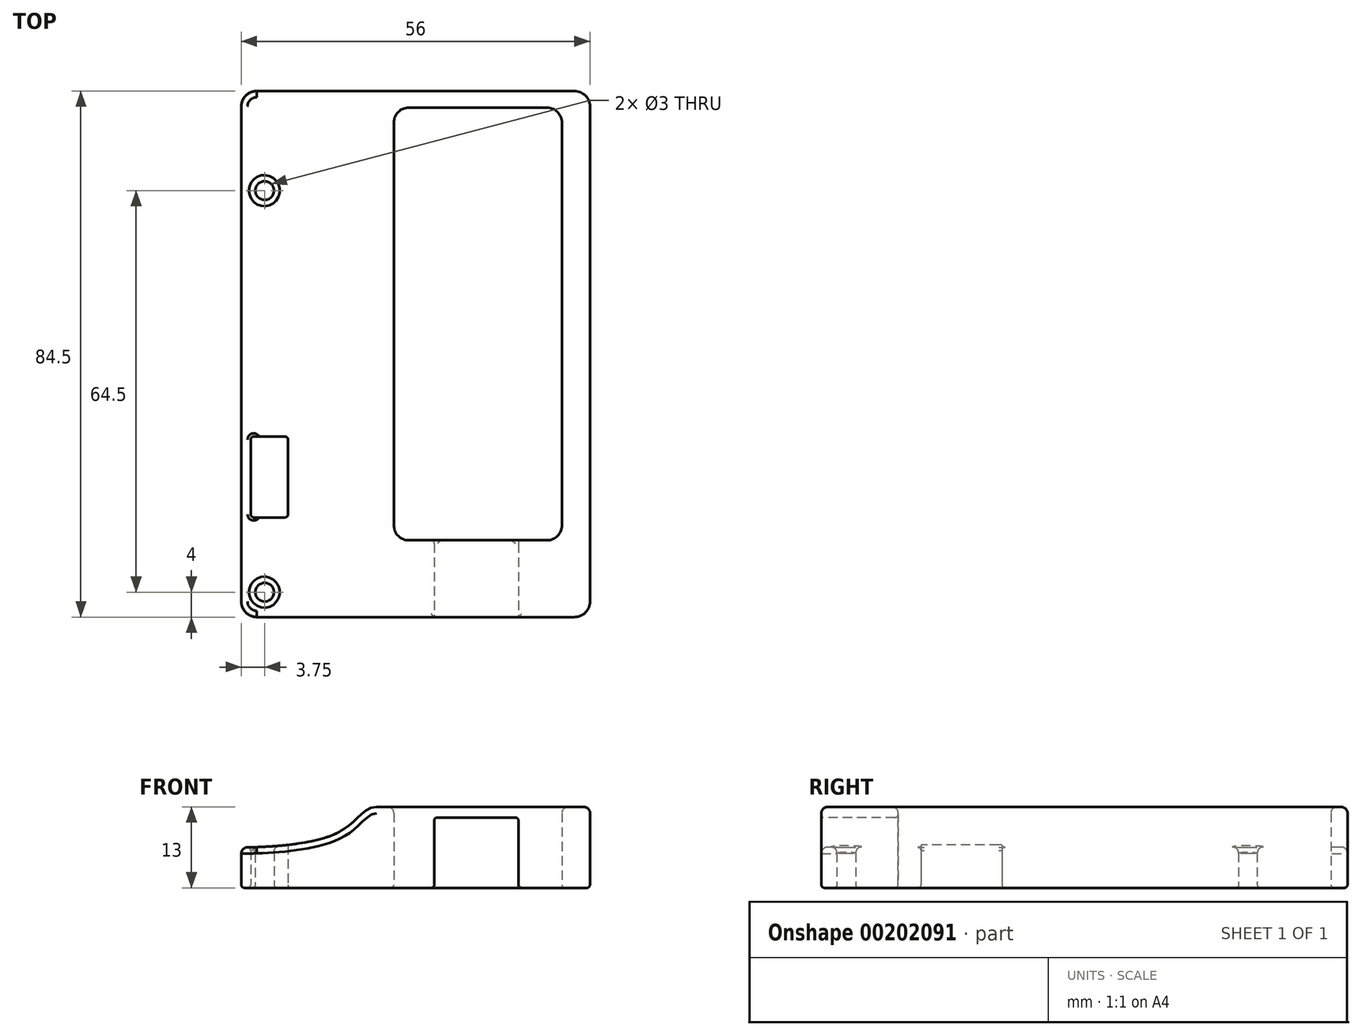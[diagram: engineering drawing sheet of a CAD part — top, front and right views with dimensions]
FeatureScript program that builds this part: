
annotation { "Feature Type Name" : "Feature", "Feature Type Description" : "" }
export const myFeature = defineFeature(function(context is Context, id is Id, definition is map)
    precondition{}
    {
        {
            var Q0;
            Q0=qCreatedBy(makeId("Top.planeOp"),FACE);
            var sketch = newSketch(context, id + "F0", { "sketchPlane" : qUnion([Q0])});
            skLineSegment(sketch, "E0.bottom", {"start": v(25.5, 36.25) * mm, "end": v(-25.5, 36.25) * mm});
            skLineSegment(sketch, "E0.top", {"start": v(25.5, -36.25) * mm, "end": v(-25.5, -36.25) * mm});
            skLineSegment(sketch, "E0.left", {"start": v(28, 33.75) * mm, "end": v(28, -33.75) * mm});
            skLineSegment(sketch, "E0.right", {"start": v(-28, 33.75) * mm, "end": v(-28, -33.75) * mm});
            skPoint(sketch, "E0.middle", {"position": v(0, 0) * mm});
            skPoint(sketch, "E1.visualSharp", {"position": v(-28, 36.25) * mm});
            skArc(sketch, "E1.filletArc", {"start": v(-25.5, 36.25) * mm, "mid": v(-27.27, 35.52) * mm, "end": v(-28, 33.75) * mm});
            skPoint(sketch, "E2.visualSharp", {"position": v(28, 36.25) * mm});
            skArc(sketch, "E2.filletArc", {"start": v(28, 33.75) * mm, "mid": v(27.27, 35.52) * mm, "end": v(25.5, 36.25) * mm});
            skPoint(sketch, "E3.visualSharp", {"position": v(28, -36.25) * mm});
            skArc(sketch, "E3.filletArc", {"start": v(25.5, -36.25) * mm, "mid": v(27.27, -35.52) * mm, "end": v(28, -33.75) * mm});
            skPoint(sketch, "E4.visualSharp", {"position": v(-28, -36.25) * mm});
            skArc(sketch, "E4.filletArc", {"start": v(-28, -33.75) * mm, "mid": v(-27.27, -35.52) * mm, "end": v(-25.5, -36.25) * mm});
            skLineSegment(sketch, "E5.bottom", {"start": v(24.25, 32.25) * mm, "end": v(-24.25, 32.25) * mm, "construction": true});
            skLineSegment(sketch, "E5.top", {"start": v(24.25, -32.25) * mm, "end": v(-24.25, -32.25) * mm, "construction": true});
            skLineSegment(sketch, "E5.left", {"start": v(24.25, 32.25) * mm, "end": v(24.25, -32.25) * mm, "construction": true});
            skLineSegment(sketch, "E5.right", {"start": v(-24.25, 32.25) * mm, "end": v(-24.25, -32.25) * mm, "construction": true});
            skCircle(sketch, "E6", {"center": v(-24.25, 32.25) * mm, "radius": 1.5 * mm});
            skCircle(sketch, "E7", {"center": v(24.25, 32.25) * mm, "radius": 1.5 * mm});
            skCircle(sketch, "E8", {"center": v(24.25, -32.25) * mm, "radius": 1.5 * mm});
            skCircle(sketch, "E9", {"center": v(-24.25, -32.25) * mm, "radius": 1.5 * mm});
            skLineSegment(sketch, "E10", {"start": v(-28, 33.75) * mm, "end": v(-28, 45.75) * mm});
            skLineSegment(sketch, "E11", {"start": v(-25.5, 48.25) * mm, "end": v(25.5, 48.25) * mm});
            skLineSegment(sketch, "E12", {"start": v(28, 45.75) * mm, "end": v(28, 33.75) * mm});
            skPoint(sketch, "E13.visualSharp", {"position": v(-28, 48.25) * mm});
            skArc(sketch, "E13.filletArc", {"start": v(-25.5, 48.25) * mm, "mid": v(-27.27, 47.52) * mm, "end": v(-28, 45.75) * mm});
            skPoint(sketch, "E14.visualSharp", {"position": v(28, 48.25) * mm});
            skArc(sketch, "E14.filletArc", {"start": v(28, 45.75) * mm, "mid": v(27.27, 47.52) * mm, "end": v(25.5, 48.25) * mm});
            skSolve(sketch);
        }
        {
            var Q0;
            Q0 = qSketchRegion(id + "F0", true);
            var Q1;
            Q1=makeQuery(id+"F0.imprint","IMPRINT",FACE,{"disambiguationData":[TD([[makeQuery(id+"F0.imprint","IMPRINT",EDGE,{"derivedFrom":sQuery(id+"F0.wireOp",EDGE,"E7")}),1.0]])]});
            var Q2;
            Q2=makeQuery(id+"F0.imprint","IMPRINT",FACE,{"disambiguationData":[TD([[makeQuery(id+"F0.imprint","IMPRINT",EDGE,{"derivedFrom":sQuery(id+"F0.wireOp",EDGE,"E8")}),1.0]])]});
            extrude(context, id + "F1", {"entities" : qUnion([Q0, Q1, Q2]), "depth" : 13 * mm});
        }
        {
            var Q0;
            Q0=makeQuery(id+"F1.opExtrude","SWEPT_FACE",FACE,{"disambiguationData":[OSD([sQuery(id+"F0.wireOp",EDGE,"E0.top")])]});
            var sketch = newSketch(context, id + "F2", { "sketchPlane" : qUnion([Q0])});
            skPoint(sketch, "E15.2.internal.snap0", {"position": v(-25.5, 6.5) * mm});
            skFitSpline(sketch, "E15", {"points": [v(-6.26, 13) * mm, v(-12.41, 8.9) * mm, v(-28, 6.5) * mm], "startDerivative": vector(-16.32, 0) * mm, "endDerivative": vector(-12.63, 0) * mm});
            skLineSegment(sketch, "E16.0", {"start": v(-28, 13) * mm, "end": v(-28, 6.5) * mm});
            skLineSegment(sketch, "E17", {"start": v(-28, 13) * mm, "end": v(-6.26, 13) * mm});
            skPoint(sketch, "E18.orphan", {"position": v(-28, 0) * mm});
            skSolve(sketch);
        }
        {
            var Q0;
            Q0 = qSketchRegion(id + "F2", true);
            extrude(context, id + "F3", {"entities" : qUnion([Q0]), "operationType" : NewBodyOperationType.REMOVE, "endBound" : BoundingType.THROUGH_ALL, "oppositeDirection" : true, "depth" : 25 * mm});
        }
        {
            var Q0;
            Q0=makeQuery(id+"F1.opExtrude","CAP_FACE",FACE,{"disambiguationData":[OSD([sQuery(id+"F0.wireOp",EDGE,"E0.top"),sQuery(id+"F0.wireOp",EDGE,"E0.left"),sQuery(id+"F0.wireOp",EDGE,"E0.right"),sQuery(id+"F0.wireOp",EDGE,"E3.filletArc"),sQuery(id+"F0.wireOp",EDGE,"E4.filletArc"),sQuery(id+"F0.wireOp",EDGE,"E6"),sQuery(id+"F0.wireOp",EDGE,"E7"),sQuery(id+"F0.wireOp",EDGE,"E8"),sQuery(id+"F0.wireOp",EDGE,"E9"),sQuery(id+"F0.wireOp",EDGE,"E10"),sQuery(id+"F0.wireOp",EDGE,"E11"),sQuery(id+"F0.wireOp",EDGE,"E12"),sQuery(id+"F0.wireOp",EDGE,"E13.filletArc"),sQuery(id+"F0.wireOp",EDGE,"E14.filletArc")])],"isStart":true});
            var sketch = newSketch(context, id + "F4", { "sketchPlane" : qUnion([Q0])});
            skLineSegment(sketch, "E19.bottom", {"start": v(3, 19.25) * mm, "end": v(16.5, 19.25) * mm});
            skLineSegment(sketch, "E19.top", {"start": v(3, 36.25) * mm, "end": v(16.5, 36.25) * mm});
            skLineSegment(sketch, "E19.left", {"start": v(3, 19.25) * mm, "end": v(3, 36.25) * mm});
            skLineSegment(sketch, "E19.right", {"start": v(16.5, 19.25) * mm, "end": v(16.5, 36.25) * mm});
            skPoint(sketch, "E19.middle", {"position": v(9.75, 27.75) * mm});
            skLineSegment(sketch, "E20.bottom", {"start": v(-3.5, -45.58) * mm, "end": v(23.5, -45.58) * mm});
            skLineSegment(sketch, "E20.top", {"start": v(-3.5, 23.92) * mm, "end": v(23.5, 23.92) * mm});
            skLineSegment(sketch, "E20.left", {"start": v(-3.5, -45.58) * mm, "end": v(-3.5, 23.92) * mm});
            skLineSegment(sketch, "E20.right", {"start": v(23.5, -45.58) * mm, "end": v(23.5, 23.92) * mm});
            skPoint(sketch, "E20.middle", {"position": v(10, -10.83) * mm});
            skSolve(sketch);
        }
        {
            var Q0;
            {var subQ0=sQuery(id+"F4.wireOp",EDGE,"E19.top");Q0=makeQuery(id+"F4.imprint","IMPRINT",FACE,{"disambiguationData":[TD([[makeQuery(id+"F4.imprint","IMPRINT",EDGE,{"derivedFrom":subQ0}),1.0]])]});}
            var Q1;
            {var subQ0=sQuery(id+"F4.wireOp",EDGE,"E19.bottom");Q1=makeQuery(id+"F4.imprint","IMPRINT",FACE,{"disambiguationData":[TD([[makeQuery(id+"F4.imprint","IMPRINT",EDGE,{"derivedFrom":subQ0}),1.0]])]});}
            extrude(context, id + "F5", {"entities" : qUnion([Q0, Q1]), "operationType" : NewBodyOperationType.REMOVE, "oppositeDirection" : true, "depth" : 11.3 * mm});
        }
        {
            var Q0;
            {var subQ2=sQuery(id+"F4.wireOp",EDGE,"E19.bottom");Q0=makeQuery(id+"F4.imprint","IMPRINT",FACE,{"disambiguationData":[TD([[makeQuery(id+"F4.imprint","IMPRINT",EDGE,{"derivedFrom":subQ2}),-1.0]])]});}
            var Q1;
            {var subQ0=sQuery(id+"F4.wireOp",EDGE,"E19.bottom");Q1=makeQuery(id+"F4.imprint","IMPRINT",FACE,{"disambiguationData":[TD([[makeQuery(id+"F4.imprint","IMPRINT",EDGE,{"derivedFrom":subQ0}),1.0]])]});}
            extrude(context, id + "F6", {"entities" : qUnion([Q0, Q1]), "operationType" : NewBodyOperationType.REMOVE, "endBound" : BoundingType.THROUGH_ALL, "oppositeDirection" : true, "depth" : 25 * mm});
        }
        {
            var Q0;
            Q0=makeQuery(id+"F6.boolean.opBoolean","COPY",EDGE,{"derivedFrom":makeQuery(id+"F6.opExtrude","SWEPT_EDGE",EDGE,{"disambiguationData":[OSD([sQuery(id+"F4.wireOp",EDGE,"E20.bottom"),sQuery(id+"F4.wireOp",EDGE,"E20.left")])]})});
            var Q1;
            Q1=makeQuery(id+"F6.boolean.opBoolean","COPY",EDGE,{"derivedFrom":makeQuery(id+"F6.opExtrude","SWEPT_EDGE",EDGE,{"disambiguationData":[OSD([sQuery(id+"F4.wireOp",EDGE,"E20.bottom"),sQuery(id+"F4.wireOp",EDGE,"E20.right")])]})});
            var Q2;
            Q2=makeQuery(id+"F6.boolean.opBoolean","COPY",EDGE,{"derivedFrom":makeQuery(id+"F6.opExtrude","SWEPT_EDGE",EDGE,{"disambiguationData":[OSD([sQuery(id+"F4.wireOp",EDGE,"E20.top"),sQuery(id+"F4.wireOp",EDGE,"E20.right")])]})});
            var Q3;
            Q3=makeQuery(id+"F6.boolean.opBoolean","COPY",EDGE,{"derivedFrom":makeQuery(id+"F6.opExtrude","SWEPT_EDGE",EDGE,{"disambiguationData":[OSD([sQuery(id+"F4.wireOp",EDGE,"E20.top"),sQuery(id+"F4.wireOp",EDGE,"E20.left")])]})});
            fillet(context, id + "F7", {"entities" : qUnion([Q0, Q1, Q2, Q3]), "radius" : 2.4 * mm, "tangentPropagation" : true, "allowEdgeOverflow" : false});
        }
        {
            var Q0;
            Q0=makeQuery(id+"F4.imprint","IMPRINT",FACE,{"disambiguationData":[TD([[makeQuery(id+"F4.imprint","IMPRINT",EDGE,{"derivedFrom":sQuery(id+"F4.wireOp",EDGE,"E20.bottom")}),-1.0]])]});
            var sketch = newSketch(context, id + "F8", { "sketchPlane" : qUnion([Q0])});
            skLineSegment(sketch, "E21.bottom", {"start": v(-26.5, 20.25) * mm, "end": v(-20.5, 20.25) * mm});
            skLineSegment(sketch, "E21.top", {"start": v(-26.5, 7.25) * mm, "end": v(-20.5, 7.25) * mm});
            skLineSegment(sketch, "E21.left", {"start": v(-26.5, 20.25) * mm, "end": v(-26.5, 7.25) * mm});
            skLineSegment(sketch, "E21.right", {"start": v(-20.5, 20.25) * mm, "end": v(-20.5, 7.25) * mm});
            skPoint(sketch, "E21.middle", {"position": v(-23.5, 13.75) * mm});
            skSolve(sketch);
        }
        {
            var Q0;
            Q0 = qSketchRegion(id + "F8", true);
            extrude(context, id + "F9", {"entities" : qUnion([Q0]), "operationType" : NewBodyOperationType.REMOVE, "endBound" : BoundingType.THROUGH_ALL, "oppositeDirection" : true, "depth" : 25 * mm});
        }
        {
            var Q0;
            Q0=makeQuery(id+"F6.boolean.opBoolean","INTERSECT",EDGE,{"derivedFrom":[makeQuery(id+"F5.boolean.opBoolean","COPY",FACE,{"derivedFrom":makeQuery(id+"F5.opExtrude","SWEPT_FACE",FACE,{"disambiguationData":[OSD([sQuery(id+"F4.wireOp",EDGE,"E19.left")])]})}),makeQuery(id+"F6.opExtrude","SWEPT_FACE",FACE,{"disambiguationData":[OSD([sQuery(id+"F4.wireOp",EDGE,"E20.top")])]})]});
            var Q1;
            Q1=makeQuery(id+"F6.boolean.opBoolean","INTERSECT",EDGE,{"derivedFrom":[makeQuery(id+"F5.boolean.opBoolean","COPY",FACE,{"derivedFrom":makeQuery(id+"F5.opExtrude","SWEPT_FACE",FACE,{"disambiguationData":[OSD([sQuery(id+"F4.wireOp",EDGE,"E19.right")])]})}),makeQuery(id+"F6.opExtrude","SWEPT_FACE",FACE,{"disambiguationData":[OSD([sQuery(id+"F4.wireOp",EDGE,"E20.top")])]})]});
            var Q2;
            Q2=makeQuery(id+"F5.boolean.opBoolean","COPY",EDGE,{"derivedFrom":makeQuery(id+"F5.opExtrude","SWEPT_EDGE",EDGE,{"disambiguationData":[OSD([sQuery(id+"F0.wireOp",EDGE,"E0.top"),sQuery(id+"F4.wireOp",EDGE,"E19.top"),sQuery(id+"F4.wireOp",EDGE,"E19.left")])]})});
            var Q3;
            Q3=makeQuery(id+"F5.boolean.opBoolean","COPY",EDGE,{"derivedFrom":makeQuery(id+"F5.opExtrude","SWEPT_EDGE",EDGE,{"disambiguationData":[OSD([sQuery(id+"F0.wireOp",EDGE,"E0.top"),sQuery(id+"F4.wireOp",EDGE,"E19.top"),sQuery(id+"F4.wireOp",EDGE,"E19.right")])]})});
            var Q4;
            Q4=makeQuery(id+"F1.opExtrude","CAP_FACE",FACE,{"disambiguationData":[OSD([sQuery(id+"F0.wireOp",EDGE,"E0.top"),sQuery(id+"F0.wireOp",EDGE,"E0.left"),sQuery(id+"F0.wireOp",EDGE,"E0.right"),sQuery(id+"F0.wireOp",EDGE,"E3.filletArc"),sQuery(id+"F0.wireOp",EDGE,"E4.filletArc"),sQuery(id+"F0.wireOp",EDGE,"E6"),sQuery(id+"F0.wireOp",EDGE,"E9"),sQuery(id+"F0.wireOp",EDGE,"E10"),sQuery(id+"F0.wireOp",EDGE,"E11"),sQuery(id+"F0.wireOp",EDGE,"E12"),sQuery(id+"F0.wireOp",EDGE,"E13.filletArc"),sQuery(id+"F0.wireOp",EDGE,"E14.filletArc")])],"isStart":true});
            var Q5;
            Q5=makeQuery(id+"F9.boolean.opBoolean","COPY",EDGE,{"derivedFrom":makeQuery(id+"F9.opExtrude","SWEPT_EDGE",EDGE,{"disambiguationData":[OSD([sQuery(id+"F8.wireOp",EDGE,"E21.top"),sQuery(id+"F8.wireOp",EDGE,"E21.right")])]})});
            var Q6;
            Q6=makeQuery(id+"F9.boolean.opBoolean","COPY",EDGE,{"derivedFrom":makeQuery(id+"F9.opExtrude","SWEPT_EDGE",EDGE,{"disambiguationData":[OSD([sQuery(id+"F8.wireOp",EDGE,"E21.top"),sQuery(id+"F8.wireOp",EDGE,"E21.left")])]})});
            var Q7;
            Q7=makeQuery(id+"F9.boolean.opBoolean","COPY",EDGE,{"derivedFrom":makeQuery(id+"F9.opExtrude","SWEPT_EDGE",EDGE,{"disambiguationData":[OSD([sQuery(id+"F8.wireOp",EDGE,"E21.bottom"),sQuery(id+"F8.wireOp",EDGE,"E21.left")])]})});
            var Q8;
            Q8=makeQuery(id+"F9.boolean.opBoolean","COPY",EDGE,{"derivedFrom":makeQuery(id+"F9.opExtrude","SWEPT_EDGE",EDGE,{"disambiguationData":[OSD([sQuery(id+"F8.wireOp",EDGE,"E21.bottom"),sQuery(id+"F8.wireOp",EDGE,"E21.right")])]})});
            var Q9;
            Q9=makeQuery(id+"F9.boolean.opBoolean","INTERSECT",EDGE,{"derivedFrom":[makeQuery(id+"F3.boolean.opBoolean","COPY",FACE,{"derivedFrom":makeQuery(id+"F3.opExtrude","SWEPT_FACE",FACE,{"disambiguationData":[OSD([sQuery(id+"F2.wireOp",EDGE,"E15")])]})}),makeQuery(id+"F9.opExtrude","SWEPT_FACE",FACE,{"disambiguationData":[OSD([sQuery(id+"F8.wireOp",EDGE,"E21.left")])]})]});
            var Q10;
            Q10=makeQuery(id+"F5.boolean.opBoolean","COPY",EDGE,{"derivedFrom":makeQuery(id+"F5.opExtrude","CAP_EDGE",EDGE,{"disambiguationData":[OSD([sQuery(id+"F4.wireOp",EDGE,"E19.right")])],"isStart":false})});
            var Q11;
            Q11=makeQuery(id+"F5.boolean.opBoolean","COPY",EDGE,{"derivedFrom":makeQuery(id+"F5.opExtrude","CAP_EDGE",EDGE,{"disambiguationData":[OSD([sQuery(id+"F4.wireOp",EDGE,"E19.left")])],"isStart":false})});
            fillet(context, id + "F10", {"entities" : qUnion([Q0, Q1, Q2, Q3, Q4, Q5, Q6, Q7, Q8, Q9, Q10, Q11]), "radius" : .5 * mm, "tangentPropagation" : true, "allowEdgeOverflow" : false});
        }
        {
            var Q0;
            Q0=makeQuery(id+"F1.opExtrude","CAP_EDGE",EDGE,{"disambiguationData":[OSD([sQuery(id+"F0.wireOp",EDGE,"E0.top")])],"isStart":false});
            fillet(context, id + "F11", {"entities" : qUnion([Q0]), "radius" : 1 * mm, "tangentPropagation" : true, "allowEdgeOverflow" : false});
        }
        {
            var Q0;
            Q0=makeQuery(id+"F7.opFillet","BLEND_EDGE",EDGE,{"blendedFrom":[makeQuery(id+"F6.boolean.opBoolean","COPY",EDGE,{"derivedFrom":makeQuery(id+"F6.opExtrude","SWEPT_EDGE",EDGE,{"disambiguationData":[OSD([sQuery(id+"F4.wireOp",EDGE,"E20.top"),sQuery(id+"F4.wireOp",EDGE,"E20.left")])]})}),makeQuery(id+"F1.opExtrude","CAP_FACE",FACE,{"disambiguationData":[OSD([sQuery(id+"F0.wireOp",EDGE,"E0.top"),sQuery(id+"F0.wireOp",EDGE,"E0.left"),sQuery(id+"F0.wireOp",EDGE,"E0.right"),sQuery(id+"F0.wireOp",EDGE,"E3.filletArc"),sQuery(id+"F0.wireOp",EDGE,"E4.filletArc"),sQuery(id+"F0.wireOp",EDGE,"E6"),sQuery(id+"F0.wireOp",EDGE,"E9"),sQuery(id+"F0.wireOp",EDGE,"E10"),sQuery(id+"F0.wireOp",EDGE,"E11"),sQuery(id+"F0.wireOp",EDGE,"E12"),sQuery(id+"F0.wireOp",EDGE,"E13.filletArc"),sQuery(id+"F0.wireOp",EDGE,"E14.filletArc")])],"isStart":false})],"blendedInto":[makeQuery(id+"F1.opExtrude","CAP_FACE",FACE,{"disambiguationData":[OSD([sQuery(id+"F0.wireOp",EDGE,"E0.top"),sQuery(id+"F0.wireOp",EDGE,"E0.left"),sQuery(id+"F0.wireOp",EDGE,"E0.right"),sQuery(id+"F0.wireOp",EDGE,"E3.filletArc"),sQuery(id+"F0.wireOp",EDGE,"E4.filletArc"),sQuery(id+"F0.wireOp",EDGE,"E6"),sQuery(id+"F0.wireOp",EDGE,"E9"),sQuery(id+"F0.wireOp",EDGE,"E10"),sQuery(id+"F0.wireOp",EDGE,"E11"),sQuery(id+"F0.wireOp",EDGE,"E12"),sQuery(id+"F0.wireOp",EDGE,"E13.filletArc"),sQuery(id+"F0.wireOp",EDGE,"E14.filletArc")])],"isStart":false})]});
            var Q1;
            Q1=makeQuery(id+"F1.opExtrude","SWEPT_FACE",FACE,{"disambiguationData":[OSD([sQuery(id+"F0.wireOp",EDGE,"E9")])]});
            var Q2;
            Q2=makeQuery(id+"F1.opExtrude","SWEPT_FACE",FACE,{"disambiguationData":[OSD([sQuery(id+"F0.wireOp",EDGE,"E6")])]});
            fillet(context, id + "F12", {"entities" : qUnion([Q0, Q1, Q2]), "radius" : 1 * mm, "tangentPropagation" : true, "allowEdgeOverflow" : false});
        }
    });
